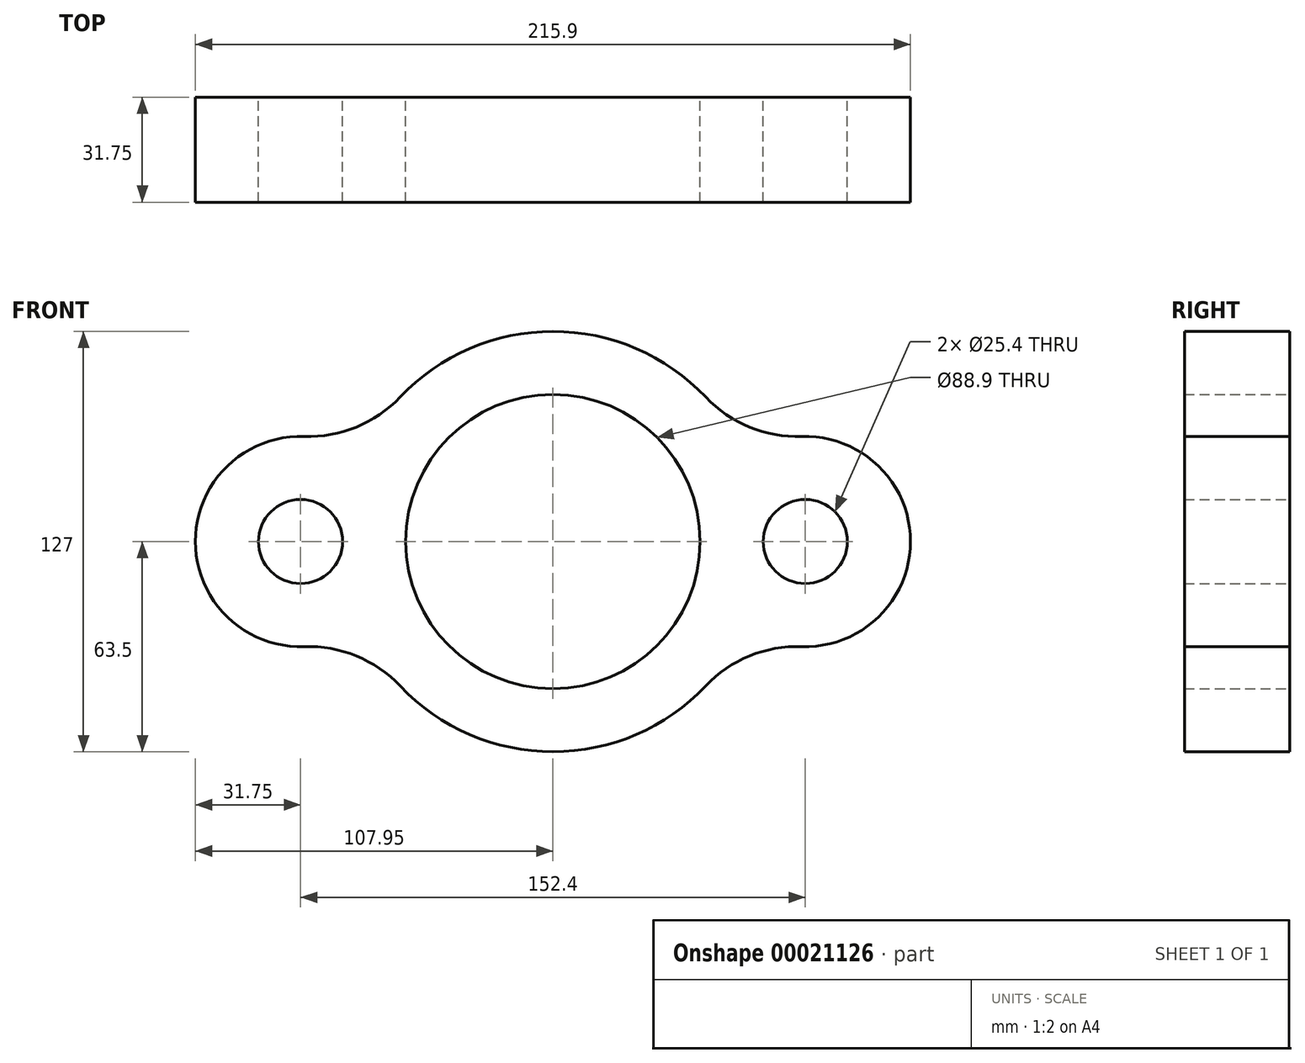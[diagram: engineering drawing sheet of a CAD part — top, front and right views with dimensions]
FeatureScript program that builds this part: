
annotation { "Feature Type Name" : "Feature", "Feature Type Description" : "" }
export const myFeature = defineFeature(function(context is Context, id is Id, definition is map)
    precondition{}
    {
        {
            var Q0;
            Q0=qCreatedBy(makeId("Front.planeOp"),FACE);
            var sketch = newSketch(context, id + "F0", { "sketchPlane" : qUnion([Q0])});
            skCircle(sketch, "E0", {"center": v(0, 0) * mm, "radius": 44.45 * mm});
            skCircle(sketch, "E1", {"center": v(76.2, 0) * mm, "radius": 12.7 * mm});
            skCircle(sketch, "E2", {"center": v(-76.2, 0) * mm, "radius": 12.7 * mm});
            skCircle(sketch, "E3", {"center": v(-76.2, 0) * mm, "radius": 31.75 * mm});
            skCircle(sketch, "E4", {"center": v(76.2, 0) * mm, "radius": 31.75 * mm});
            skCircle(sketch, "E5", {"center": v(0, 0) * mm, "radius": 63.5 * mm});
            skCircle(sketch, "E6", {"center": v(-73.82, 69.8) * mm, "radius": 38.1 * mm});
            skCircle(sketch, "E7", {"center": v(73.82, -69.8) * mm, "radius": 38.1 * mm});
            skCircle(sketch, "E8", {"center": v(73.82, 69.8) * mm, "radius": 38.1 * mm});
            skCircle(sketch, "E9", {"center": v(-73.82, -69.8) * mm, "radius": 38.1 * mm});
            skSolve(sketch);
        }
        {
            var Q0;
            {var subQ0=sQuery(id+"F0.wireOp",EDGE,"E6");var subQ3=sQuery(id+"F0.wireOp",EDGE,"E3");var subQ4=makeQuery(id+"F0.imprint","INTERSECT",VERTEX,{"derivedFrom":[subQ3,subQ0]});Q0=makeQuery(id+"F0.imprint","IMPRINT",FACE,{"disambiguationData":[TD([[makeQuery(id+"F0.imprint","IMPRINT",EDGE,{"disambiguationData":[TD([[subQ4,1.0]])],"derivedFrom":subQ3}),-1.0]])]});}
            var Q1;
            {var subQ0=sQuery(id+"F0.wireOp",EDGE,"E8");var subQ3=sQuery(id+"F0.wireOp",EDGE,"E4");var subQ4=makeQuery(id+"F0.imprint","INTERSECT",VERTEX,{"derivedFrom":[subQ3,subQ0]});Q1=makeQuery(id+"F0.imprint","IMPRINT",FACE,{"disambiguationData":[TD([[makeQuery(id+"F0.imprint","IMPRINT",EDGE,{"disambiguationData":[TD([[subQ4,-1.0]])],"derivedFrom":subQ3}),-1.0]])]});}
            var Q2;
            {var subQ0=sQuery(id+"F0.wireOp",EDGE,"E7");var subQ3=sQuery(id+"F0.wireOp",EDGE,"E4");var subQ4=makeQuery(id+"F0.imprint","INTERSECT",VERTEX,{"derivedFrom":[subQ3,subQ0]});Q2=makeQuery(id+"F0.imprint","IMPRINT",FACE,{"disambiguationData":[TD([[makeQuery(id+"F0.imprint","IMPRINT",EDGE,{"disambiguationData":[TD([[subQ4,1.0]])],"derivedFrom":subQ3}),-1.0]])]});}
            var Q3;
            {var subQ0=sQuery(id+"F0.wireOp",EDGE,"E9");var subQ3=sQuery(id+"F0.wireOp",EDGE,"E3");var subQ4=makeQuery(id+"F0.imprint","INTERSECT",VERTEX,{"derivedFrom":[subQ3,subQ0]});Q3=makeQuery(id+"F0.imprint","IMPRINT",FACE,{"disambiguationData":[TD([[makeQuery(id+"F0.imprint","IMPRINT",EDGE,{"disambiguationData":[TD([[subQ4,-1.0]])],"derivedFrom":subQ3}),-1.0]])]});}
            var Q4;
            {var subQ3=sQuery(id+"F0.wireOp",EDGE,"E3");var subQ7=sQuery(id+"F0.wireOp",EDGE,"E0");var subQ9=makeQuery(id+"F0.imprint","INTERSECT",VERTEX,{"derivedFrom":[subQ7,subQ3]});Q4=makeQuery(id+"F0.imprint","IMPRINT",FACE,{"disambiguationData":[TD([[makeQuery(id+"F0.imprint","IMPRINT",EDGE,{"disambiguationData":[TD([[subQ9,-1.0]])],"derivedFrom":subQ7}),-1.0]])]});}
            var Q5;
            {var subQ1=sQuery(id+"F0.wireOp",EDGE,"E4");var subQ5=makeQuery(id+"F0.imprint","INTERSECT",VERTEX,{"derivedFrom":[sQuery(id+"F0.wireOp",EDGE,"E0"),subQ1]});Q5=makeQuery(id+"F0.imprint","IMPRINT",FACE,{"disambiguationData":[TD([[makeQuery(id+"F0.imprint","IMPRINT",EDGE,{"disambiguationData":[TD([[subQ5,1.0]])],"derivedFrom":subQ1}),1.0]])]});}
            var Q6;
            {var subQ3=sQuery(id+"F0.wireOp",EDGE,"E1");Q6=makeQuery(id+"F0.imprint","IMPRINT",FACE,{"disambiguationData":[TD([[makeQuery(id+"F0.imprint","IMPRINT",EDGE,{"derivedFrom":subQ3}),-1.0]])]});}
            var Q7;
            {var subQ5=sQuery(id+"F0.wireOp",EDGE,"E3");var subQ7=sQuery(id+"F0.wireOp",EDGE,"E0");var subQ9=makeQuery(id+"F0.imprint","INTERSECT",VERTEX,{"derivedFrom":[subQ7,subQ5]});Q7=makeQuery(id+"F0.imprint","IMPRINT",FACE,{"disambiguationData":[TD([[makeQuery(id+"F0.imprint","IMPRINT",EDGE,{"disambiguationData":[TD([[subQ9,1.0]])],"derivedFrom":subQ7}),-1.0]])]});}
            var Q8;
            {var subQ1=sQuery(id+"F0.wireOp",EDGE,"E3");var subQ5=makeQuery(id+"F0.imprint","INTERSECT",VERTEX,{"derivedFrom":[sQuery(id+"F0.wireOp",EDGE,"E0"),subQ1]});Q8=makeQuery(id+"F0.imprint","IMPRINT",FACE,{"disambiguationData":[TD([[makeQuery(id+"F0.imprint","IMPRINT",EDGE,{"disambiguationData":[TD([[subQ5,-1.0]])],"derivedFrom":subQ1}),1.0]])]});}
            var Q9;
            {var subQ3=sQuery(id+"F0.wireOp",EDGE,"E2");Q9=makeQuery(id+"F0.imprint","IMPRINT",FACE,{"disambiguationData":[TD([[makeQuery(id+"F0.imprint","IMPRINT",EDGE,{"derivedFrom":subQ3}),-1.0]])]});}
            extrude(context, id + "F1", {"entities" : qUnion([Q0, Q1, Q2, Q3, Q4, Q5, Q6, Q7, Q8, Q9]), "depth" : 31.75 * mm});
        }
    });
